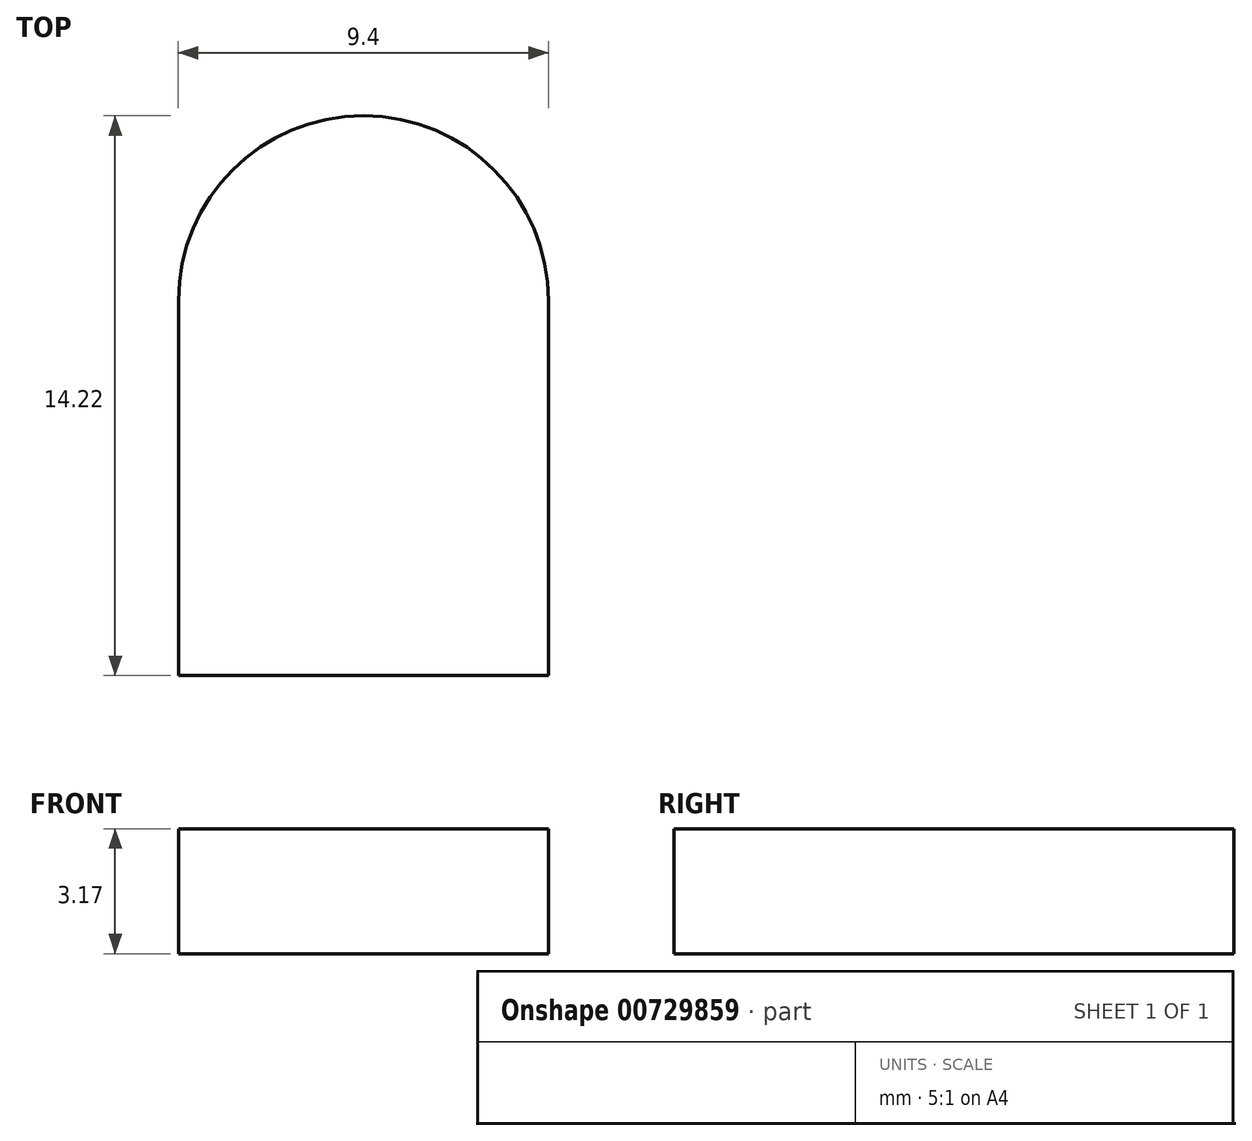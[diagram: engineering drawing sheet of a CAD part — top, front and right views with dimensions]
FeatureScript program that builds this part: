
annotation { "Feature Type Name" : "Feature", "Feature Type Description" : "" }
export const myFeature = defineFeature(function(context is Context, id is Id, definition is map)
    precondition{}
    {
        {
            var Q0;
            Q0=qCreatedBy(makeId("Top.planeOp"),FACE);
            var sketch = newSketch(context, id + "F0", { "sketchPlane" : qUnion([Q0])});
            skLineSegment(sketch, "E0.bottom", {"start": v(-22.29, -30.2) * mm, "end": v(-12.89, -30.2) * mm});
            skLineSegment(sketch, "E0.top", {"start": v(-22.29, -39.73) * mm, "end": v(-12.89, -39.73) * mm});
            skLineSegment(sketch, "E0.left", {"start": v(-22.29, -30.2) * mm, "end": v(-22.29, -39.73) * mm});
            skLineSegment(sketch, "E0.right", {"start": v(-12.89, -30.2) * mm, "end": v(-12.89, -39.73) * mm});
            skCircle(sketch, "E1", {"center": v(-17.59, -30.2) * mm, "radius": 4.7 * mm});
            skSolve(sketch);
        }
        {
            var Q0;
            Q0=makeQuery(id+"F0.imprint","IMPRINT",FACE,{"disambiguationData":[TD([[makeQuery(id+"F0.imprint","IMPRINT",EDGE,{"derivedFrom":sQuery(id+"F0.wireOp",EDGE,"E0.top")}),1.0]])]});
            var Q1;
            {var subQ0=sQuery(id+"F0.wireOp",EDGE,"E0.bottom");Q1=makeQuery(id+"F0.imprint","IMPRINT",FACE,{"disambiguationData":[TD([[makeQuery(id+"F0.imprint","IMPRINT",EDGE,{"derivedFrom":subQ0}),-1.0]])]});}
            var Q2;
            {var subQ0=sQuery(id+"F0.wireOp",EDGE,"E0.bottom");Q2=makeQuery(id+"F0.imprint","IMPRINT",FACE,{"disambiguationData":[TD([[makeQuery(id+"F0.imprint","IMPRINT",EDGE,{"derivedFrom":subQ0}),1.0]])]});}
            extrude(context, id + "F1", {"entities" : qUnion([Q0, Q1, Q2]), "depth" : 3.17 * mm, "offsetDistance" : 25.4 * mm});
        }
    });
